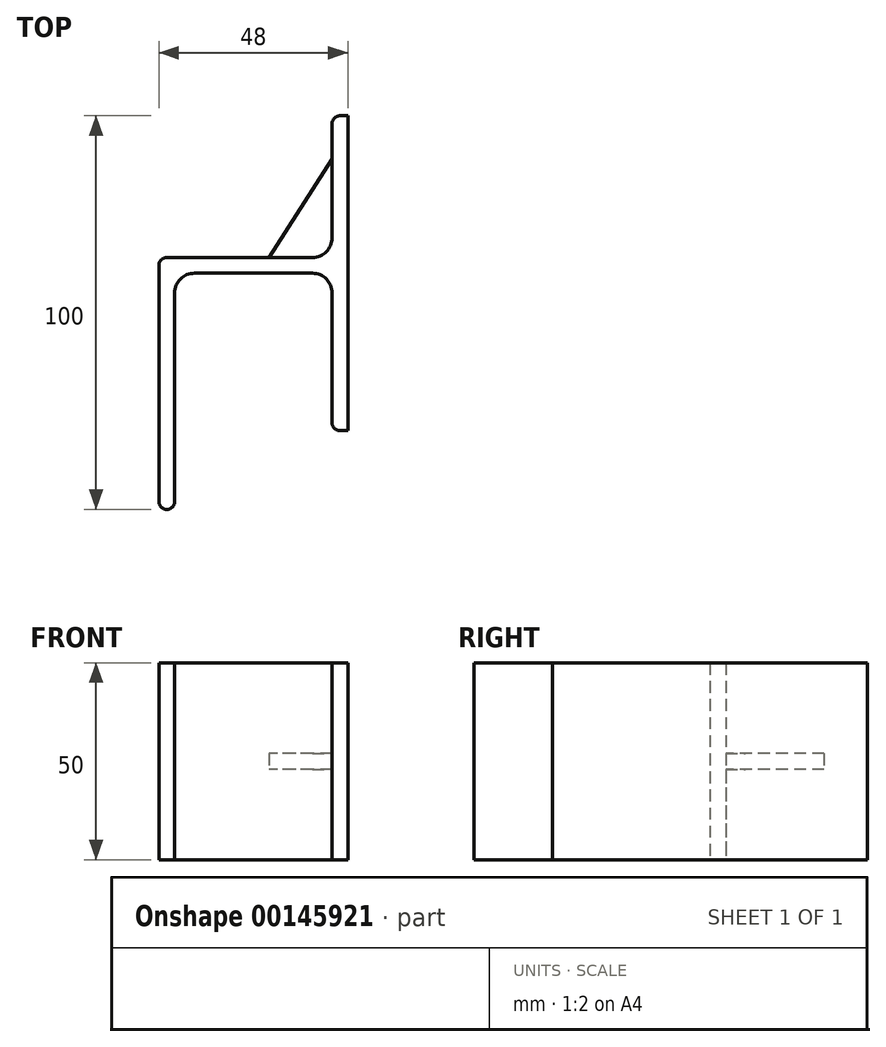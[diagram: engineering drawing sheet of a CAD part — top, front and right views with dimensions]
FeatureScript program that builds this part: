
annotation { "Feature Type Name" : "Feature", "Feature Type Description" : "" }
export const myFeature = defineFeature(function(context is Context, id is Id, definition is map)
    precondition{}
    {
        {
            var Q0;
            Q0=qCreatedBy(makeId("Top.planeOp"),FACE);
            var sketch = newSketch(context, id + "F0", { "sketchPlane" : qUnion([Q0])});
            skLineSegment(sketch, "E0.bottom", {"start": v(0, 40) * mm, "end": v(4, 40) * mm});
            skLineSegment(sketch, "E0.top", {"start": v(0, -40) * mm, "end": v(4, -40) * mm});
            skLineSegment(sketch, "E0.left", {"start": v(0, 40) * mm, "end": v(0, -40) * mm});
            skLineSegment(sketch, "E0.right", {"start": v(4, 40) * mm, "end": v(4, -40) * mm});
            skPoint(sketch, "E1.oppositeSnap0", {"position": v(4, 0) * mm});
            skLineSegment(sketch, "E1.bottom", {"start": v(0, 4) * mm, "end": v(-40, 4) * mm});
            skLineSegment(sketch, "E1.top", {"start": v(0, 0) * mm, "end": v(-40, 0) * mm});
            skLineSegment(sketch, "E1.left", {"start": v(0, 4) * mm, "end": v(0, 0) * mm});
            skLineSegment(sketch, "E1.right", {"start": v(-40, 4) * mm, "end": v(-40, 0) * mm});
            skLineSegment(sketch, "E2.bottom", {"start": v(-44, 4) * mm, "end": v(-40, 4) * mm});
            skLineSegment(sketch, "E2.top", {"start": v(-44, -60) * mm, "end": v(-40, -60) * mm});
            skLineSegment(sketch, "E2.left", {"start": v(-44, 4) * mm, "end": v(-44, -60) * mm});
            skLineSegment(sketch, "E2.right", {"start": v(-40, 0) * mm, "end": v(-40, -60) * mm});
            skLineSegment(sketch, "E3", {"start": v(0, 29) * mm, "end": v(-16, 4) * mm});
            skSolve(sketch);
        }
        {
            var Q0;
            Q0=makeQuery(id+"F0.imprint","IMPRINT",FACE,{"disambiguationData":[TD([[makeQuery(id+"F0.imprint","IMPRINT",EDGE,{"derivedFrom":sQuery(id+"F0.wireOp",EDGE,"E1.right")}),-1.0]])]});
            var Q1;
            Q1=makeQuery(id+"F0.imprint","IMPRINT",FACE,{"disambiguationData":[TD([[makeQuery(id+"F0.imprint","IMPRINT",EDGE,{"derivedFrom":sQuery(id+"F0.wireOp",EDGE,"E1.top")}),-1.0]])]});
            var Q2;
            {var subQ3=sQuery(id+"F0.wireOp",EDGE,"E0.bottom");Q2=makeQuery(id+"F0.imprint","IMPRINT",FACE,{"disambiguationData":[TD([[makeQuery(id+"F0.imprint","IMPRINT",EDGE,{"derivedFrom":subQ3}),-1.0]])]});}
            extrude(context, id + "F1", {"entities" : qUnion([Q0, Q1, Q2]), "depth" : 25 * mm});
        }
        {
            var Q0;
            {var subQ3=sQuery(id+"F0.wireOp",EDGE,"E0.bottom");Q0=makeQuery(id+"F0.imprint","IMPRINT",FACE,{"disambiguationData":[TD([[makeQuery(id+"F0.imprint","IMPRINT",EDGE,{"derivedFrom":subQ3}),-1.0]])]});}
            var Q1;
            Q1=makeQuery(id+"F0.imprint","IMPRINT",FACE,{"disambiguationData":[TD([[makeQuery(id+"F0.imprint","IMPRINT",EDGE,{"derivedFrom":sQuery(id+"F0.wireOp",EDGE,"E1.top")}),-1.0]])]});
            var Q2;
            Q2=makeQuery(id+"F0.imprint","IMPRINT",FACE,{"disambiguationData":[TD([[makeQuery(id+"F0.imprint","IMPRINT",EDGE,{"derivedFrom":sQuery(id+"F0.wireOp",EDGE,"E1.right")}),-1.0]])]});
            extrude(context, id + "F2", {"entities" : qUnion([Q0, Q1, Q2]), "operationType" : NewBodyOperationType.ADD, "oppositeDirection" : true, "depth" : 25 * mm});
        }
        {
            var Q0;
            {var subQ3=sQuery(id+"F0.wireOp",EDGE,"E3");Q0=makeQuery(id+"F0.imprint","IMPRINT",FACE,{"disambiguationData":[TD([[makeQuery(id+"F0.imprint","IMPRINT",EDGE,{"derivedFrom":subQ3}),1.0]])]});}
            extrude(context, id + "F3", {"entities" : qUnion([Q0]), "operationType" : NewBodyOperationType.ADD, "depth" : 2 * mm, "hasSecondDirection" : true, "secondDirectionOppositeDirection" : true, "secondDirectionDepth" : 2 * mm});
        }
        {
            var Q0;
            {var subQ0=sQuery(id+"F0.wireOp",EDGE,"E2.right");var subQ1=sQuery(id+"F0.wireOp",EDGE,"E1.right");var subQ2=sQuery(id+"F0.wireOp",EDGE,"E1.top");Q0=makeQuery(id+"F2.boolean.opBoolean","MERGE",EDGE,{"derivedFrom":[makeQuery(id+"F1.opExtrude","SWEPT_EDGE",EDGE,{"disambiguationData":[OSD([subQ2,subQ1,subQ0])]}),makeQuery(id+"F2.opExtrude","SWEPT_EDGE",EDGE,{"disambiguationData":[OSD([subQ2,subQ1,subQ0])]})]});}
            var Q1;
            {var subQ0=sQuery(id+"F0.wireOp",EDGE,"E1.left");var subQ1=sQuery(id+"F0.wireOp",EDGE,"E1.top");var subQ2=sQuery(id+"F0.wireOp",EDGE,"E0.left");Q1=makeQuery(id+"F2.boolean.opBoolean","MERGE",EDGE,{"derivedFrom":[makeQuery(id+"F1.opExtrude","SWEPT_EDGE",EDGE,{"disambiguationData":[OSD([subQ2,subQ1,subQ0])]}),makeQuery(id+"F2.opExtrude","SWEPT_EDGE",EDGE,{"disambiguationData":[OSD([subQ2,subQ1,subQ0])]})]});}
            var Q2;
            {var subQ0=sQuery(id+"F0.wireOp",EDGE,"E1.left");var subQ1=sQuery(id+"F0.wireOp",EDGE,"E1.bottom");var subQ2=sQuery(id+"F0.wireOp",EDGE,"E0.left");var subQ3=sQuery(id+"F0.wireOp",EDGE,"E3");Q2=makeQuery(id+"F3.boolean.opBoolean","SPLIT",EDGE,{"disambiguationData":[TD([makeQuery(id+"F3.opExtrude","CAP_FACE",FACE,{"disambiguationData":[OSD([subQ2,subQ1,subQ3])],"isStart":false})])],"derivedFrom":makeQuery(id+"F2.boolean.opBoolean","MERGE",EDGE,{"derivedFrom":[makeQuery(id+"F1.opExtrude","SWEPT_EDGE",EDGE,{"disambiguationData":[OSD([subQ2,subQ1,subQ0])]}),makeQuery(id+"F2.opExtrude","SWEPT_EDGE",EDGE,{"disambiguationData":[OSD([subQ2,subQ1,subQ0])]})]})});}
            var Q3;
            {var subQ0=sQuery(id+"F0.wireOp",EDGE,"E1.left");var subQ1=sQuery(id+"F0.wireOp",EDGE,"E1.bottom");var subQ2=sQuery(id+"F0.wireOp",EDGE,"E0.left");var subQ3=sQuery(id+"F0.wireOp",EDGE,"E3");Q3=makeQuery(id+"F3.boolean.opBoolean","SPLIT",EDGE,{"disambiguationData":[TD([makeQuery(id+"F3.opExtrude","CAP_FACE",FACE,{"disambiguationData":[OSD([subQ2,subQ1,subQ3])],"isStart":true})])],"derivedFrom":makeQuery(id+"F2.boolean.opBoolean","MERGE",EDGE,{"derivedFrom":[makeQuery(id+"F1.opExtrude","SWEPT_EDGE",EDGE,{"disambiguationData":[OSD([subQ2,subQ1,subQ0])]}),makeQuery(id+"F2.opExtrude","SWEPT_EDGE",EDGE,{"disambiguationData":[OSD([subQ2,subQ1,subQ0])]})]})});}
            fillet(context, id + "F4", {"entities" : qUnion([Q0, Q1, Q2, Q3]), "radius" : 5 * mm, "tangentPropagation" : true, "allowEdgeOverflow" : false});
        }
        {
            var Q0;
            {var subQ0=sQuery(id+"F0.wireOp",EDGE,"E2.left");var subQ1=sQuery(id+"F0.wireOp",EDGE,"E2.bottom");Q0=makeQuery(id+"F2.boolean.opBoolean","MERGE",EDGE,{"derivedFrom":[makeQuery(id+"F1.opExtrude","SWEPT_EDGE",EDGE,{"disambiguationData":[OSD([subQ1,subQ0])]}),makeQuery(id+"F2.opExtrude","SWEPT_EDGE",EDGE,{"disambiguationData":[OSD([subQ1,subQ0])]})]});}
            var Q1;
            {var subQ0=sQuery(id+"F0.wireOp",EDGE,"E0.left");var subQ1=sQuery(id+"F0.wireOp",EDGE,"E0.bottom");Q1=makeQuery(id+"F2.boolean.opBoolean","MERGE",EDGE,{"derivedFrom":[makeQuery(id+"F1.opExtrude","SWEPT_EDGE",EDGE,{"disambiguationData":[OSD([subQ1,subQ0])]}),makeQuery(id+"F2.opExtrude","SWEPT_EDGE",EDGE,{"disambiguationData":[OSD([subQ1,subQ0])]})]});}
            var Q2;
            {var subQ0=sQuery(id+"F0.wireOp",EDGE,"E2.left");var subQ1=sQuery(id+"F0.wireOp",EDGE,"E2.top");Q2=makeQuery(id+"F2.boolean.opBoolean","MERGE",EDGE,{"derivedFrom":[makeQuery(id+"F1.opExtrude","SWEPT_EDGE",EDGE,{"disambiguationData":[OSD([subQ1,subQ0])]}),makeQuery(id+"F2.opExtrude","SWEPT_EDGE",EDGE,{"disambiguationData":[OSD([subQ1,subQ0])]})]});}
            var Q3;
            {var subQ0=sQuery(id+"F0.wireOp",EDGE,"E2.right");var subQ1=sQuery(id+"F0.wireOp",EDGE,"E2.top");Q3=makeQuery(id+"F2.boolean.opBoolean","MERGE",EDGE,{"derivedFrom":[makeQuery(id+"F1.opExtrude","SWEPT_EDGE",EDGE,{"disambiguationData":[OSD([subQ1,subQ0])]}),makeQuery(id+"F2.opExtrude","SWEPT_EDGE",EDGE,{"disambiguationData":[OSD([subQ1,subQ0])]})]});}
            var Q4;
            {var subQ0=sQuery(id+"F0.wireOp",EDGE,"E0.left");var subQ1=sQuery(id+"F0.wireOp",EDGE,"E0.top");Q4=makeQuery(id+"F2.boolean.opBoolean","MERGE",EDGE,{"derivedFrom":[makeQuery(id+"F1.opExtrude","SWEPT_EDGE",EDGE,{"disambiguationData":[OSD([subQ1,subQ0])]}),makeQuery(id+"F2.opExtrude","SWEPT_EDGE",EDGE,{"disambiguationData":[OSD([subQ1,subQ0])]})]});}
            var Q5;
            Q5=makeQuery(id+"F3.opExtrude","SWEPT_EDGE",EDGE,{"disambiguationData":[OSD([sQuery(id+"F0.wireOp",EDGE,"E1.bottom"),sQuery(id+"F0.wireOp",EDGE,"E3")])]});
            var Q6;
            Q6=makeQuery(id+"F3.opExtrude","SWEPT_EDGE",EDGE,{"disambiguationData":[OSD([sQuery(id+"F0.wireOp",EDGE,"E0.left"),sQuery(id+"F0.wireOp",EDGE,"E3")])]});
            fillet(context, id + "F5", {"entities" : qUnion([Q0, Q1, Q2, Q3, Q4, Q5, Q6]), "radius" : 2 * mm, "tangentPropagation" : true, "allowEdgeOverflow" : false});
        }
    });
